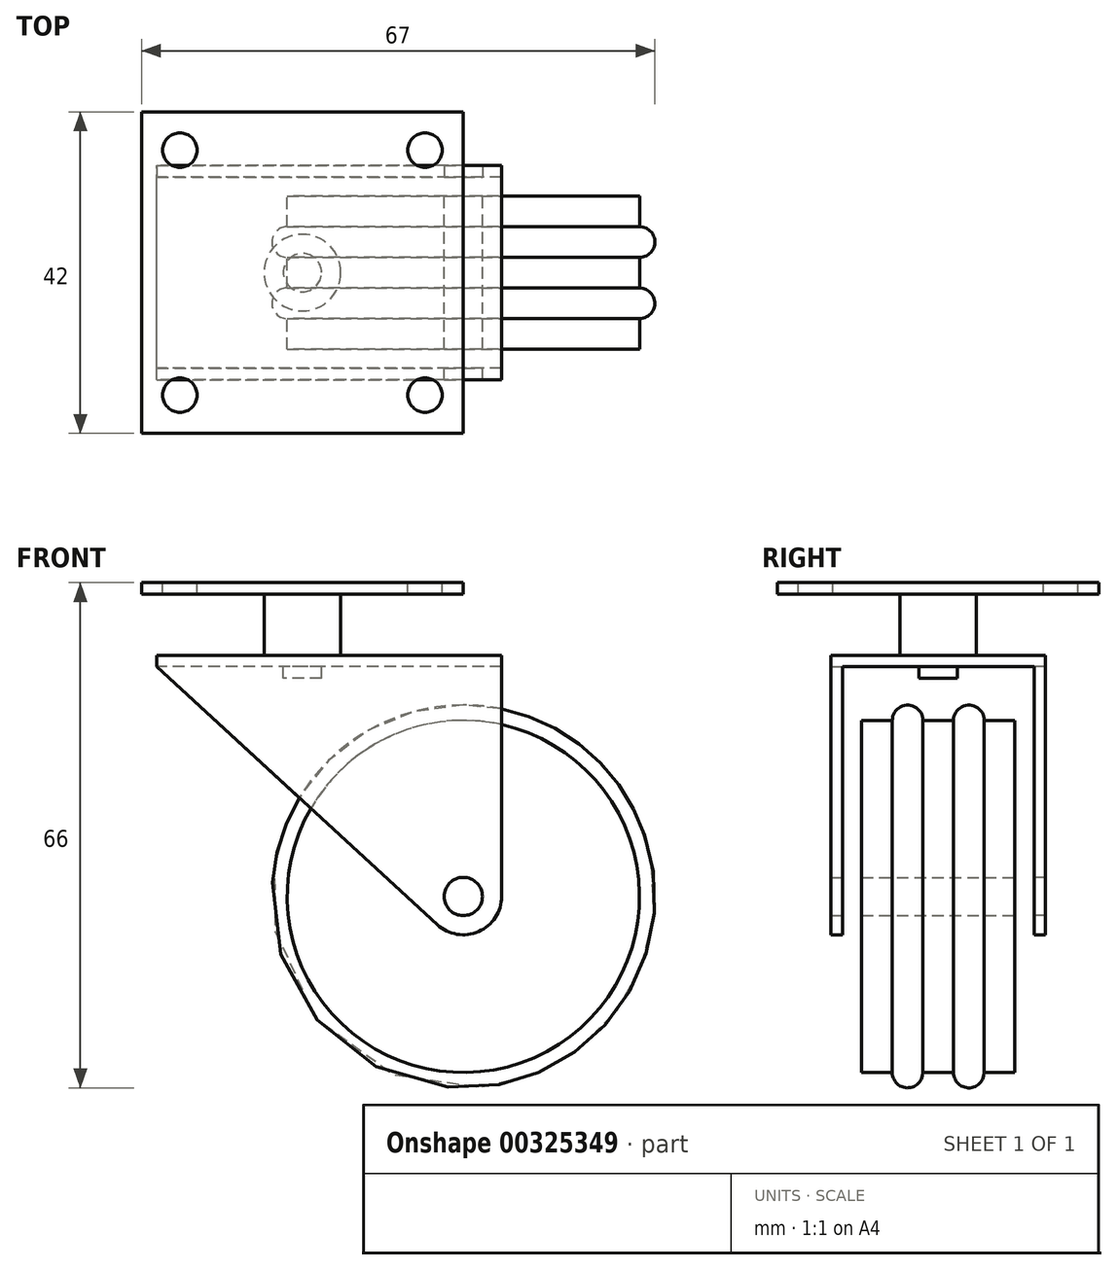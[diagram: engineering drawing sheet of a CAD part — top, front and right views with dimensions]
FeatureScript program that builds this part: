
annotation { "Feature Type Name" : "Feature", "Feature Type Description" : "" }
export const myFeature = defineFeature(function(context is Context, id is Id, definition is map)
    precondition{}
    {
        {
            var Q0;
            Q0=qCreatedBy(makeId("Top.planeOp"),FACE);
            var sketch = newSketch(context, id + "F0", { "sketchPlane" : qUnion([Q0])});
            skLineSegment(sketch, "E0.bottom", {"start": v(-23, 10) * mm, "end": v(-2.5, 10) * mm});
            skLineSegment(sketch, "E0.top", {"start": v(-23, -10) * mm, "end": v(-2.5, -10) * mm});
            skPoint(sketch, "E0.middle", {"position": v(0, 0) * mm});
            skLineSegment(sketch, "E1", {"start": v(0, 10) * mm, "end": v(0, -10) * mm, "construction": true});
            skPoint(sketch, "E0.right.end.orphan", {"position": v(25, -10) * mm});
            skPoint(sketch, "E0.right.start.orphan", {"position": v(25, 10) * mm});
            skLineSegment(sketch, "E2", {"start": v(-2.5, 10) * mm, "end": v(-2.5, -10) * mm});
            skPoint(sketch, "E3.start.orphan", {"position": v(0, 17.65) * mm});
            skArc(sketch, "E4", {"start": v(-23, 6) * mm, "mid": v(-25, 4) * mm, "end": v(-23, 2) * mm});
            skArc(sketch, "E5.MirrorC", {"start": v(-23, -6) * mm, "mid": v(-25, -4) * mm, "end": v(-23, -2) * mm});
            skLineSegment(sketch, "E6", {"start": v(-23, -10) * mm, "end": v(-23, -6) * mm});
            skPoint(sketch, "E7.orphan", {"position": v(-25, 10) * mm});
            skPoint(sketch, "E8.orphan", {"position": v(-25, -10) * mm});
            skPoint(sketch, "E9.orphan", {"position": v(-23, -11.78) * mm});
            skLineSegment(sketch, "E10.trimOffspring", {"start": v(-23, 6) * mm, "end": v(-23, 10) * mm});
            skLineSegment(sketch, "E11.trimOffspring", {"start": v(-23, -2) * mm, "end": v(-23, 2) * mm});
            skSolve(sketch);
        }
        {
            var Q0;
            Q0 = qSketchRegion(id + "F0", true);
            var Q1;
            Q1=sQuery(id+"F0.wireOp",EDGE,"E1");
            revolve(context, id + "F1", {"entities" : qUnion([Q0]), "axis" : qUnion([Q1]), "revolveType" : RevolveType.FULL});
        }
        {
            var Q0;
            Q0=makeQuery(id+"F1.opRevolve","SWEPT_FACE",FACE,{"disambiguationData":[OSD([sQuery(id+"F0.wireOp",EDGE,"E0.bottom")])]});
            cPlane(context, id + "F2", {"entities" : qUnion([Q0]), "cplaneType" : CPlaneType.OFFSET, "offset" : 2.5 * mm, "width" : 150 * mm, "height" : 150 * mm});
        }
        {
            var Q0;
            Q0=qCreatedBy(id+"F2.planeOp",FACE);
            var sketch = newSketch(context, id + "F3", { "sketchPlane" : qUnion([Q0])});
            skCircle(sketch, "E12.0", {"center": v(0, 0) * mm, "radius": 2.5 * mm});
            skArc(sketch, "E13", {"start": v(-5, 0) * mm, "mid": v(-2, -4.58) * mm, "end": v(3.38, -3.68) * mm});
            skLineSegment(sketch, "E14", {"start": v(-5, 0) * mm, "end": v(-5, 30) * mm});
            skLineSegment(sketch, "E15", {"start": v(-5, 30) * mm, "end": v(40, 30) * mm});
            skLineSegment(sketch, "E16", {"start": v(40, 30) * mm, "end": v(3.38, -3.68) * mm});
            skSolve(sketch);
        }
        {
            var Q0;
            Q0 = qSketchRegion(id + "F3", true);
            extrude(context, id + "F4", {"entities" : qUnion([Q0]), "depth" : 1.5 * mm});
        }
        {
            var Q0;
            Q0=makeQuery(id+"F4.opExtrude","SWEPT_BODY",BODY,{"disambiguationData":[OSD([sQuery(id+"F3.wireOp",EDGE,"E12.0"),sQuery(id+"F3.wireOp",EDGE,"E13"),sQuery(id+"F3.wireOp",EDGE,"E14"),sQuery(id+"F3.wireOp",EDGE,"E15"),sQuery(id+"F3.wireOp",EDGE,"E16")])]});
            var Q1;
            Q1=qCreatedBy(makeId("Front.planeOp"),FACE);
            mirror(context, id + "F5", {"entities" : qUnion([Q0]), "mirrorPlane" : qUnion([Q1])});
        }
        {
            var Q0;
            Q0=makeQuery(id+"F5.opPattern","COPY",FACE,{"derivedFrom":makeQuery(id+"F4.opExtrude","SWEPT_FACE",FACE,{"disambiguationData":[OSD([sQuery(id+"F3.wireOp",EDGE,"E15")])]}),"instanceName":"1"});
            var sketch = newSketch(context, id + "F6", { "sketchPlane" : qUnion([Q0])});
            skLineSegment(sketch, "E17.0", {"start": v(5, 14) * mm, "end": v(-40, 14) * mm});
            skLineSegment(sketch, "E17.1", {"start": v(5, -14) * mm, "end": v(-40, -14) * mm});
            skLineSegment(sketch, "E18", {"start": v(5, -14) * mm, "end": v(5, 14) * mm});
            skLineSegment(sketch, "E19", {"start": v(-40, -14) * mm, "end": v(-40, 14) * mm});
            skSolve(sketch);
        }
        {
            var Q0;
            Q0 = qSketchRegion(id + "F6", true);
            extrude(context, id + "F7", {"entities" : qUnion([Q0]), "operationType" : NewBodyOperationType.ADD, "depth" : 1.5 * mm});
        }
        {
            var Q0;
            Q0=makeQuery(id+"F7.opExtrude","CAP_FACE",FACE,{"disambiguationData":[OSD([sQuery(id+"F6.wireOp",EDGE,"E17.0"),sQuery(id+"F6.wireOp",EDGE,"E17.1"),sQuery(id+"F6.wireOp",EDGE,"E18"),sQuery(id+"F6.wireOp",EDGE,"E19")])],"isStart":false});
            var sketch = newSketch(context, id + "F8", { "sketchPlane" : qUnion([Q0])});
            skCircle(sketch, "E20", {"center": v(-21, 0) * mm, "radius": 2.5 * mm});
            skSolve(sketch);
        }
        {
            var Q0;
            Q0 = qSketchRegion(id + "F8", true);
            extrude(context, id + "F9", {"entities" : qUnion([Q0]), "operationType" : NewBodyOperationType.REMOVE, "oppositeDirection" : true, "depth" : 1.5 * mm});
        }
        {
            var Q0;
            Q0=makeQuery(id+"F7.opExtrude","CAP_FACE",FACE,{"disambiguationData":[OSD([sQuery(id+"F6.wireOp",EDGE,"E17.0"),sQuery(id+"F6.wireOp",EDGE,"E17.1"),sQuery(id+"F6.wireOp",EDGE,"E18"),sQuery(id+"F6.wireOp",EDGE,"E19")])],"isStart":false});
            var sketch = newSketch(context, id + "F10", { "sketchPlane" : qUnion([Q0])});
            skCircle(sketch, "E21", {"center": v(-21, 0) * mm, "radius": 2.5 * mm});
            skSolve(sketch);
        }
        {
            var Q0;
            Q0 = qSketchRegion(id + "F10", true);
            extrude(context, id + "F11", {"entities" : qUnion([Q0]), "oppositeDirection" : true, "depth" : 3 * mm});
        }
        {
            var Q0;
            Q0=makeQuery(id+"F11.opExtrude","CAP_FACE",FACE,{"disambiguationData":[OSD([sQuery(id+"F10.wireOp",EDGE,"E21")])],"isStart":true});
            var sketch = newSketch(context, id + "F12", { "sketchPlane" : qUnion([Q0])});
            skCircle(sketch, "E22", {"center": v(-21, 0) * mm, "radius": 5 * mm});
            skSolve(sketch);
        }
        {
            var Q0;
            Q0 = qSketchRegion(id + "F12", true);
            extrude(context, id + "F13", {"entities" : qUnion([Q0]), "operationType" : NewBodyOperationType.ADD, "depth" : 9.5 * mm});
        }
        {
            var Q0;
            Q0=makeQuery(id+"F13.opExtrude","CAP_FACE",FACE,{"disambiguationData":[OSD([sQuery(id+"F12.wireOp",EDGE,"E22")])],"isStart":false});
            var sketch = newSketch(context, id + "F14", { "sketchPlane" : qUnion([Q0])});
            skLineSegment(sketch, "E23.bottom", {"start": v(-42, 21) * mm, "end": v(0, 21) * mm});
            skLineSegment(sketch, "E23.top", {"start": v(-42, -21) * mm, "end": v(0, -21) * mm});
            skLineSegment(sketch, "E23.left", {"start": v(-42, 21) * mm, "end": v(-42, -21) * mm});
            skLineSegment(sketch, "E23.right", {"start": v(0, 21) * mm, "end": v(0, -21) * mm});
            skPoint(sketch, "E23.middle", {"position": v(-21, 0) * mm});
            skCircle(sketch, "E24", {"center": v(-5, -16) * mm, "radius": 2.25 * mm});
            skLineSegment(sketch, "E25", {"start": v(-21, 0) * mm, "end": v(-21, 18.34) * mm, "construction": true});
            skLineSegment(sketch, "E26", {"start": v(-21, 0) * mm, "end": v(-33.58, 0) * mm, "construction": true});
            skCircle(sketch, "E27.MirrorC", {"center": v(-37, -16) * mm, "radius": 2.25 * mm});
            skCircle(sketch, "E28.MirrorC", {"center": v(-5, 16) * mm, "radius": 2.25 * mm});
            skCircle(sketch, "E29.MirrorC", {"center": v(-37, 16) * mm, "radius": 2.25 * mm});
            skSolve(sketch);
        }
        {
            var Q0;
            Q0 = qSketchRegion(id + "F14", true);
            extrude(context, id + "F15", {"entities" : qUnion([Q0]), "operationType" : NewBodyOperationType.ADD, "oppositeDirection" : true, "depth" : 1.5 * mm});
        }
    });
